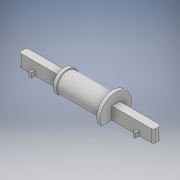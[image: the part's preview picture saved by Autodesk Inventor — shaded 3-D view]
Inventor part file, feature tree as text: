
AUTODESK INVENTOR PART (.ipt)
format: ipt  version: 2018 (Build 220112000, 112)  size: 181,760 bytes
history: native  units: mm
features: extrude x4, sketch x4, mirror x2, plane x1, thicken_offset x1, fillet x1, direct_edit x1, projected_geometry x1, move_body x1
ambient origin geometry x8: Origin, YZ Plane, XZ Plane, XY Plane, X Axis, Y Axis, Z Axis, Center Point
bodies: Solid1 (feature_tree)
feature tree (16):
  extrude  "Extrusion1"  Depth=7.0mm
  plane  "Work Plane1"
  extrude  "Extrusion2"  Depth=120.0mm TaperAngle=0.0deg
  extrude  "Extrusion3"  Depth=40.0mm TaperAngle=0.0deg
  mirror  "Mirror1"
  thicken_offset  "Thicken1"
  fillet  "Fillet1"  Radius=5.0mm
  direct_edit  "Direct Edit1"
  extrude  "Extrusion4"  Depth=4.0mm
  mirror  "Mirror2"
  sketch  "Sketch1"  dims[d0=20.0mm d1=7.0mm]
  sketch  "Sketch2"  dims[d2=10.0mm d3=120.0mm d4=0.0mm]
  sketch  "Sketch3"  dims[d5=18.0mm d6=40.0mm d7=0.0mm d8=5.0mm]
  sketch  "Sketch4"  dims[d9=3.0mm d10=0.0mm d11=4.0mm d12=4.0mm d14=0.0mm d15=0.0mm d16=1.0mm d17=2.0mm d18=95.0mm d19=14.0mm d20=2.0mm d21=4.0mm d22=0.0mm d23=12.5mm d24=12.5mm]
  projected_geometry  "Projected Loop1"
  move_body  "Move1"
